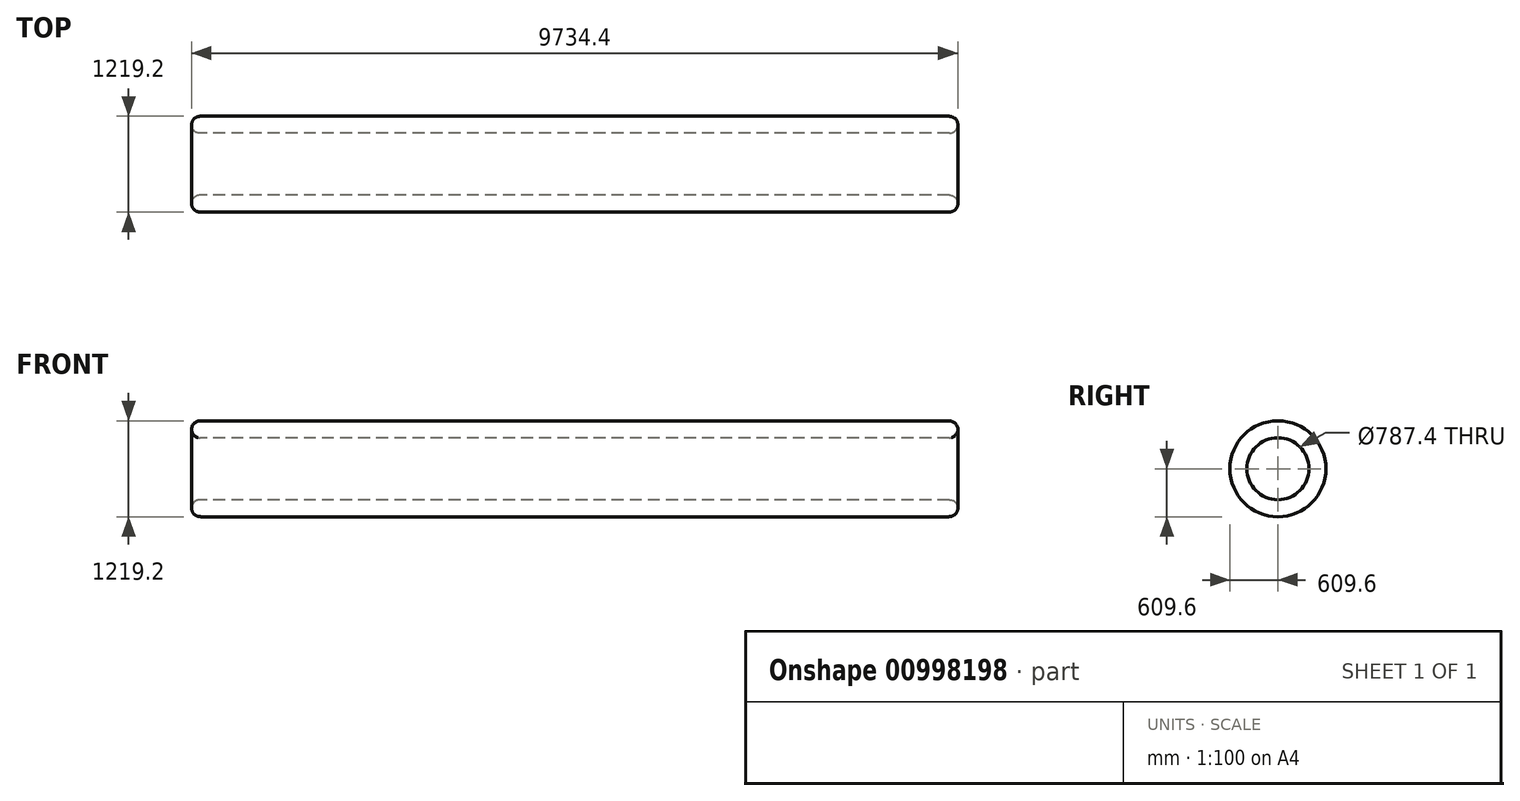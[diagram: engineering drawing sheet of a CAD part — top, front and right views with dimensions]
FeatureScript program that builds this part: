
annotation { "Feature Type Name" : "Feature", "Feature Type Description" : "" }
export const myFeature = defineFeature(function(context is Context, id is Id, definition is map)
    precondition{}
    {
        {
            var Q0;
            Q0=qCreatedBy(makeId("Right.planeOp"),FACE);
            var sketch = newSketch(context, id + "F0", { "sketchPlane" : qUnion([Q0])});
            skCircle(sketch, "E0", {"center": v(0, 0) * mm, "radius": 393.7 * mm});
            skCircle(sketch, "E1", {"center": v(0, 0) * mm, "radius": 609.6 * mm});
            skSolve(sketch);
        }
        {
            var Q0;
            Q0=makeQuery(id+"F0.imprint","IMPRINT",FACE,{"disambiguationData":[TD([[makeQuery(id+"F0.imprint","IMPRINT",EDGE,{"derivedFrom":sQuery(id+"F0.wireOp",EDGE,"E0")}),-1.0]])]});
            var Q1;
            Q1=sQuery(id+"F0.wireOp",EDGE,"E0");
            var Q2;
            Q2=sQuery(id+"F0.wireOp",EDGE,"E1");
            extrude(context, id + "F1", {"entities" : qUnion([Q0]), "surfaceEntities" : qUnion([Q1, Q2]), "depth" : 9906 * mm, "offsetDistance" : 25.4 * mm});
        }
        {
            var Q0;
            Q0=makeQuery(id+"F1.opExtrude","CAP_EDGE",EDGE,{"disambiguationData":[OSD([sQuery(id+"F0.wireOp",EDGE,"E1")])],"isStart":false});
            fillet(context, id + "F2", {"entities" : qUnion([Q0]), "radius" : 215.9 * mm, "tangentPropagation" : true, "allowEdgeOverflow" : false});
        }
        {
            var Q0;
            Q0=makeQuery(id+"F2.opFillet","BLEND_EDGE",EDGE,{"blendedFrom":[makeQuery(id+"F1.opExtrude","CAP_EDGE",EDGE,{"disambiguationData":[OSD([sQuery(id+"F0.wireOp",EDGE,"E1")])],"isStart":false}),makeQuery(id+"F1.opExtrude","SWEPT_FACE",FACE,{"disambiguationData":[OSD([sQuery(id+"F0.wireOp",EDGE,"E0")])]})],"blendedInto":[makeQuery(id+"F1.opExtrude","SWEPT_FACE",FACE,{"disambiguationData":[OSD([sQuery(id+"F0.wireOp",EDGE,"E0")])]})]});
            fillet(context, id + "F3", {"entities" : qUnion([Q0]), "radius" : 106.68 * mm, "tangentPropagation" : true, "allowEdgeOverflow" : false});
        }
        {
            var Q0;
            Q0=makeQuery(id+"F1.opExtrude","CAP_EDGE",EDGE,{"disambiguationData":[OSD([sQuery(id+"F0.wireOp",EDGE,"E1")])],"isStart":true});
            fillet(context, id + "F4", {"entities" : qUnion([Q0]), "radius" : 215.9 * mm, "tangentPropagation" : true, "allowEdgeOverflow" : false});
        }
        {
            var Q0;
            Q0=makeQuery(id+"F4.opFillet","BLEND_EDGE",EDGE,{"blendedFrom":[makeQuery(id+"F1.opExtrude","CAP_EDGE",EDGE,{"disambiguationData":[OSD([sQuery(id+"F0.wireOp",EDGE,"E1")])],"isStart":true}),makeQuery(id+"F1.opExtrude","SWEPT_FACE",FACE,{"disambiguationData":[OSD([sQuery(id+"F0.wireOp",EDGE,"E0")])]})],"blendedInto":[makeQuery(id+"F1.opExtrude","SWEPT_FACE",FACE,{"disambiguationData":[OSD([sQuery(id+"F0.wireOp",EDGE,"E0")])]})]});
            fillet(context, id + "F5", {"entities" : qUnion([Q0]), "radius" : 106.68 * mm, "tangentPropagation" : true, "allowEdgeOverflow" : false});
        }
    });
